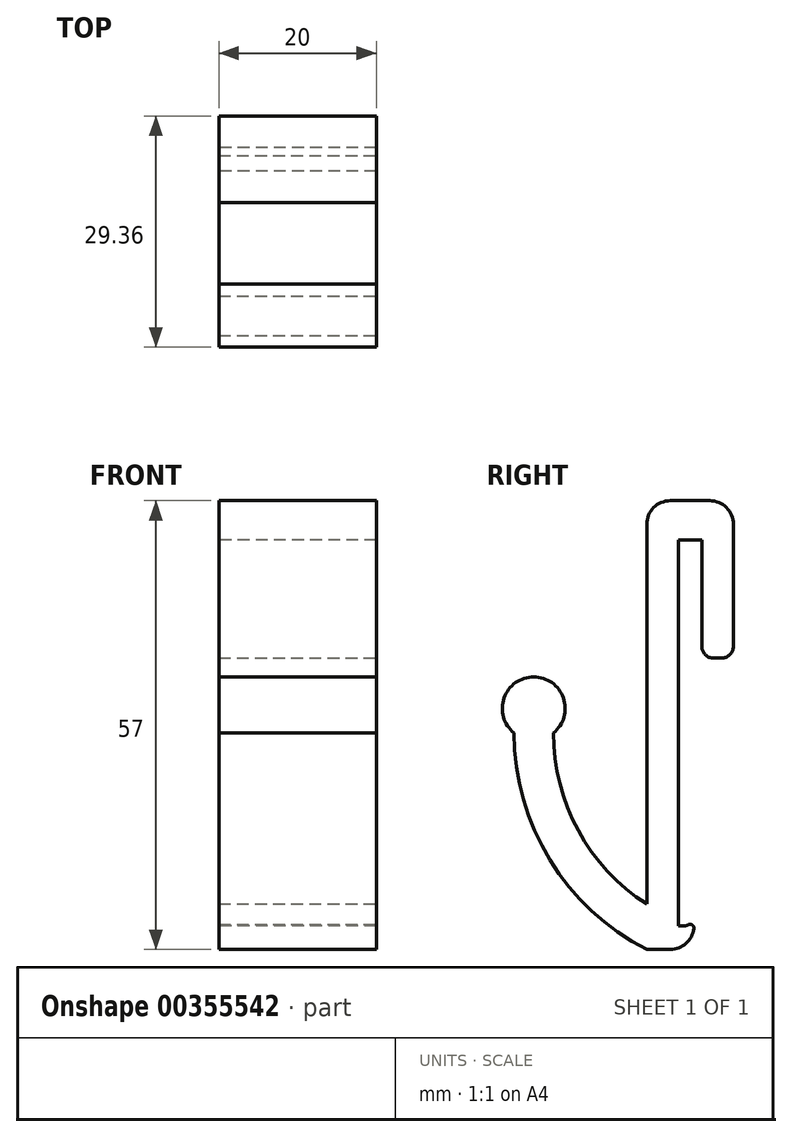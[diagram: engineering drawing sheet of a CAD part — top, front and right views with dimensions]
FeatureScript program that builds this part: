
annotation { "Feature Type Name" : "Feature", "Feature Type Description" : "" }
export const myFeature = defineFeature(function(context is Context, id is Id, definition is map)
    precondition{}
    {
        {
            var Q0;
            Q0=qCreatedBy(makeId("Front.planeOp"),FACE);
            var sketch = newSketch(context, id + "F0", { "sketchPlane" : qUnion([Q0])});
            skLineSegment(sketch, "E0.rect.bottom", {"start": v(10, -24.5) * mm, "end": v(-10, -24.5) * mm});
            skLineSegment(sketch, "E0.rect.top", {"start": v(10, 24.5) * mm, "end": v(-10, 24.5) * mm});
            skLineSegment(sketch, "E0.rect.left", {"start": v(10, -24.5) * mm, "end": v(10, 24.5) * mm});
            skLineSegment(sketch, "E0.rect.right", {"start": v(-10, -24.5) * mm, "end": v(-10, 24.5) * mm});
            skPoint(sketch, "E0.rect.middle", {"position": v(0, 0) * mm});
            skLineSegment(sketch, "E1", {"start": v(-10, 24.5) * mm, "end": v(-10, 29.5) * mm});
            skLineSegment(sketch, "E2", {"start": v(-10, 29.5) * mm, "end": v(10, 29.5) * mm});
            skLineSegment(sketch, "E3", {"start": v(10, 29.5) * mm, "end": v(10, 24.5) * mm});
            skLineSegment(sketch, "E4", {"start": v(10, -24.5) * mm, "end": v(10, -27.5) * mm});
            skLineSegment(sketch, "E5", {"start": v(10, -27.5) * mm, "end": v(-10, -27.5) * mm});
            skLineSegment(sketch, "E6", {"start": v(-10, -27.5) * mm, "end": v(-10, -24.5) * mm});
            skSolve(sketch);
        }
        {
            var Q0;
            Q0=makeQuery(id+"F0.imprint","IMPRINT",FACE,{"disambiguationData":[TD([[makeQuery(id+"F0.imprint","IMPRINT",EDGE,{"derivedFrom":sQuery(id+"F0.wireOp",EDGE,"E0.rect.bottom")}),-1.0]])]});
            var Q1;
            Q1=makeQuery(id+"F0.imprint","IMPRINT",FACE,{"disambiguationData":[TD([[makeQuery(id+"F0.imprint","IMPRINT",EDGE,{"derivedFrom":sQuery(id+"F0.wireOp",EDGE,"E0.rect.top")}),-1.0]])]});
            var Q2;
            Q2=makeQuery(id+"F0.imprint","IMPRINT",FACE,{"disambiguationData":[TD([[makeQuery(id+"F0.imprint","IMPRINT",EDGE,{"derivedFrom":sQuery(id+"F0.wireOp",EDGE,"E0.rect.bottom")}),1.0]])]});
            extrude(context, id + "F1", {"entities" : qUnion([Q0, Q1, Q2]), "depth" : 4 * mm});
        }
        {
            var Q0;
            Q0=makeQuery(id+"F0.imprint","IMPRINT",FACE,{"disambiguationData":[TD([[makeQuery(id+"F0.imprint","IMPRINT",EDGE,{"derivedFrom":sQuery(id+"F0.wireOp",EDGE,"E0.rect.top")}),-1.0]])]});
            extrude(context, id + "F2", {"entities" : qUnion([Q0]), "operationType" : NewBodyOperationType.ADD, "oppositeDirection" : true, "depth" : 3 * mm});
        }
        {
            var Q0;
            Q0=makeQuery(id+"F0.imprint","IMPRINT",FACE,{"disambiguationData":[TD([[makeQuery(id+"F0.imprint","IMPRINT",EDGE,{"derivedFrom":sQuery(id+"F0.wireOp",EDGE,"E0.rect.bottom")}),1.0]])]});
            extrude(context, id + "F3", {"entities" : qUnion([Q0]), "operationType" : NewBodyOperationType.ADD, "oppositeDirection" : true, "depth" : 1 * mm});
        }
        {
            var Q0;
            {var subQ0=sQuery(id+"F0.wireOp",EDGE,"E3");var subQ1=sQuery(id+"F0.wireOp",EDGE,"E4");Q0=makeQuery(id+"F3.boolean.opBoolean","MERGE",FACE,{"derivedFrom":[makeQuery(id+"F2.boolean.opBoolean","MERGE",FACE,{"derivedFrom":[makeQuery(id+"F1.opExtrude","SWEPT_FACE",FACE,{"disambiguationData":[OSD([sQuery(id+"F0.wireOp",EDGE,"E0.rect.left"),subQ0,subQ1])]}),makeQuery(id+"F2.opExtrude","SWEPT_FACE",FACE,{"disambiguationData":[OSD([subQ0])]})]}),makeQuery(id+"F3.opExtrude","SWEPT_FACE",FACE,{"disambiguationData":[OSD([subQ1])]})]});}
            var sketch = newSketch(context, id + "F4", { "sketchPlane" : qUnion([Q0])});
            skLineSegment(sketch, "E7", {"start": v(3, 29.5) * mm, "end": v(3, 9.5) * mm});
            skLineSegment(sketch, "E8", {"start": v(3, 9.5) * mm, "end": v(7, 9.5) * mm});
            skLineSegment(sketch, "E9", {"start": v(7, 9.5) * mm, "end": v(7, 29.5) * mm});
            skLineSegment(sketch, "E10", {"start": v(7, 29.5) * mm, "end": v(3, 29.5) * mm});
            skLineSegment(sketch, "E11", {"start": v(1, -27.5) * mm, "end": v(2, -27.5) * mm});
            skLineSegment(sketch, "E12", {"start": v(2, -27.5) * mm, "end": v(2, -23.92) * mm});
            skLineSegment(sketch, "E13", {"start": v(2, -23.92) * mm, "end": v(1, -24.5) * mm});
            skLineSegment(sketch, "E14", {"start": v(1, -24.5) * mm, "end": v(1, -27.5) * mm});
            skArc(sketch, "E15", {"start": v(-20.86, 0) * mm, "mid": v(-16.3, -16.13) * mm, "end": v(-4, -27.5) * mm});
            skArc(sketch, "E16", {"start": v(-15.86, 0) * mm, "mid": v(-12.7, -12.38) * mm, "end": v(-4, -21.74) * mm});
            skLineSegment(sketch, "E17", {"start": v(-20.86, 0) * mm, "end": v(10, 0) * mm, "construction": true});
            skArc(sketch, "E18", {"start": v(-15.86, 0) * mm, "mid": v(-18.36, 7.12) * mm, "end": v(-20.86, 0) * mm});
            skSolve(sketch);
        }
        {
            var Q0;
            Q0=qSketchRegion(id+"F4",true);
            var Q1;
            {var subQ4=sQuery(id+"F4.wireOp",EDGE,"E15");Q1=makeQuery(id+"F4.imprint","IMPRINT",FACE,{"disambiguationData":[TD([[makeQuery(id+"F4.imprint","IMPRINT",EDGE,{"derivedFrom":subQ4}),1.0]])]});}
            var Q2;
            {var subQ0=sQuery(id+"F0.wireOp",EDGE,"E1");var subQ1=sQuery(id+"F0.wireOp",EDGE,"E6");Q2=makeQuery(id+"F3.boolean.opBoolean","MERGE",FACE,{"derivedFrom":[makeQuery(id+"F2.boolean.opBoolean","MERGE",FACE,{"derivedFrom":[makeQuery(id+"F1.opExtrude","SWEPT_FACE",FACE,{"disambiguationData":[OSD([sQuery(id+"F0.wireOp",EDGE,"E0.rect.right"),subQ0,subQ1])]}),makeQuery(id+"F2.opExtrude","SWEPT_FACE",FACE,{"disambiguationData":[OSD([subQ0])]})]}),makeQuery(id+"F3.opExtrude","SWEPT_FACE",FACE,{"disambiguationData":[OSD([subQ1])]})]});}
            extrude(context, id + "F5", {"entities" : qUnion([Q0, Q1]), "operationType" : NewBodyOperationType.ADD, "endBound" : BoundingType.UP_TO_SURFACE, "oppositeDirection" : true, "endBoundEntityFace" : qUnion([Q2]), "depth" : 25 * mm});
        }
        {
            var Q0;
            Q0=makeQuery(id+"F5.opExtrude","SWEPT_EDGE",EDGE,{"disambiguationData":[OSD([sQuery(id+"F4.wireOp",EDGE,"E9"),sQuery(id+"F4.wireOp",EDGE,"E10")])]});
            var Q1;
            Q1=makeQuery(id+"F1.opExtrude","CAP_EDGE",EDGE,{"disambiguationData":[OSD([sQuery(id+"F0.wireOp",EDGE,"E2")])],"isStart":false});
            var Q2;
            Q2=makeQuery(id+"F5.opExtrude","SWEPT_EDGE",EDGE,{"disambiguationData":[OSD([sQuery(id+"F4.wireOp",EDGE,"E11"),sQuery(id+"F4.wireOp",EDGE,"E12")])]});
            var Q3;
            Q3=makeQuery(id+"F5.opExtrude","SWEPT_EDGE",EDGE,{"disambiguationData":[OSD([sQuery(id+"F0.wireOp",EDGE,"E0.rect.left"),sQuery(id+"F0.wireOp",EDGE,"E3"),sQuery(id+"F0.wireOp",EDGE,"E4"),sQuery(id+"F4.wireOp",EDGE,"ea8893f4-6408-4d1f-b56b-d2168bf36e3d")])]});
            fillet(context, id + "F6", {"entities" : qUnion([Q0, Q1, Q2, Q3]), "radius" : 3 * mm, "tangentPropagation" : true, "allowEdgeOverflow" : false});
        }
        {
            var Q0;
            Q0=makeQuery(id+"F2.opExtrude","CAP_EDGE",EDGE,{"disambiguationData":[OSD([sQuery(id+"F0.wireOp",EDGE,"E0.rect.top")])],"isStart":false});
            var Q1;
            Q1=makeQuery(id+"F2.opExtrude","CAP_EDGE",EDGE,{"disambiguationData":[OSD([sQuery(id+"F0.wireOp",EDGE,"E0.rect.top")])],"isStart":true});
            var Q2;
            Q2=makeQuery(id+"F3.opExtrude","CAP_EDGE",EDGE,{"disambiguationData":[OSD([sQuery(id+"F0.wireOp",EDGE,"E0.rect.bottom")])],"isStart":true});
            var Q3;
            {var subQ0=sQuery(id+"F0.wireOp",EDGE,"E0.rect.bottom");Q3=makeQuery(id+"F5.boolean.opBoolean","MERGE",EDGE,{"derivedFrom":[makeQuery(id+"F3.opExtrude","CAP_EDGE",EDGE,{"disambiguationData":[OSD([subQ0])],"isStart":false}),makeQuery(id+"F5.opExtrude","SWEPT_EDGE",EDGE,{"disambiguationData":[OSD([subQ0,sQuery(id+"F0.wireOp",EDGE,"E0.rect.left"),sQuery(id+"F0.wireOp",EDGE,"E4"),sQuery(id+"F4.wireOp",EDGE,"E13"),sQuery(id+"F4.wireOp",EDGE,"E14")])]})]});}
            var Q4;
            Q4=makeQuery(id+"F5.opExtrude","SWEPT_EDGE",EDGE,{"disambiguationData":[OSD([sQuery(id+"F4.wireOp",EDGE,"E12"),sQuery(id+"F4.wireOp",EDGE,"E13")])]});
            fillet(context, id + "F7", {"entities" : qUnion([Q0, Q1, Q2, Q3, Q4]), "radius" : 0.5 * mm, "tangentPropagation" : true, "allowEdgeOverflow" : false});
        }
        {
            var Q0;
            Q0=makeQuery(id+"F5.opExtrude","SWEPT_EDGE",EDGE,{"disambiguationData":[OSD([sQuery(id+"F4.wireOp",EDGE,"E7"),sQuery(id+"F4.wireOp",EDGE,"E8")])]});
            var Q1;
            Q1=makeQuery(id+"F5.opExtrude","SWEPT_EDGE",EDGE,{"disambiguationData":[OSD([sQuery(id+"F4.wireOp",EDGE,"E8"),sQuery(id+"F4.wireOp",EDGE,"E9")])]});
            var Q2;
            Q2=makeQuery(id+"F5.opExtrude","SWEPT_EDGE",EDGE,{"disambiguationData":[OSD([sQuery(id+"F4.wireOp",EDGE,"ea8893f4-6408-4d1f-b56b-d2168bf36e3d"),sQuery(id+"F4.wireOp",EDGE,"fcd73a69-4350-4eb9-ac6e-9daeea31be28")])]});
            var Q3;
            Q3=makeQuery(id+"F5.opExtrude","SWEPT_EDGE",EDGE,{"disambiguationData":[OSD([sQuery(id+"F4.wireOp",EDGE,"13445d1f-a1cf-4193-8990-ddddebb34eff"),sQuery(id+"F4.wireOp",EDGE,"fcd73a69-4350-4eb9-ac6e-9daeea31be28")])]});
            fillet(context, id + "F8", {"entities" : qUnion([Q0, Q1, Q2, Q3]), "radius" : 1.5 * mm, "tangentPropagation" : true, "allowEdgeOverflow" : false});
        }
    });
